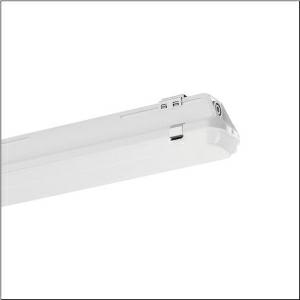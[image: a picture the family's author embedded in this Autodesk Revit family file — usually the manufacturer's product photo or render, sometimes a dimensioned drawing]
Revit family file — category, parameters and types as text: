
# Revit family: monsun_r__21_51fb107p480b_58b6
name_source: partatom
category: Lighting Fixtures
units: mm (PartAtom-declared; Revit-internal decimal feet)

## family parameters
Cut with Voids When Loaded = No
Host = Face
Light Source = No
Part Type = Normal
Room Calculation Point = No
Round Connector Dimension = Use Diameter
Shared = No

## types (1)
- Monsun® 21 (1 x LED, 8070 lm, 52.8 W, 4000K)
    Apparent Load = 53 VA
    CIE Flux Codes = 47 77 93 94 100
    Color Rendering = 80
    Color Temperature = 4000K
    Default Elevation = 1800 mm
    Description = Monsun® 21, damp-proof luminaire, chain hanger, primary optical cover: enclosure, of PMMA, light emission: direct distribution, primary light characteristic: symmetric, installation type: suspended mounting, surface-mounted, horizontal mounting, vertical mounting, LED, rated luminous flux: 8.070lm, luminous efficacy: 153lm/W, light colour: 840, colour temperature: 4000K, control gear: ECG, with terminal, 3-pole, max. 2.5mm², mains connection: 220..240V, AC, 50/60Hz, rated input power: 53W, housing, of glass-fibre reinforced polyester, uncoated, bright grey, length: 1.590mm, width: 90mm, height: 88mm, clip for enclosure, of stainless steel (V2A), ceiling mounting element, of stainless steel (V2A), chain hanger, of stainless steel (V2A), protection rating (complete): IP66, insulation class (complete): insulation class I (protective earthing), certification: CE, ENEC, VDE, UKCA, protection symbol: D, impact resistance: IK04, permissible operating ambient temperature: -25..+35°C, standard: EN 50419, EN 60598-2-1, corresponds to IFS (International Featured Standards) requirements for safety and quality in the food industry, for indoor or canopied outdoor use, no direct snow, no direct sun, no direct rain, packaging unit: 1 piece
    Height = 89 mm
    Lamp = 1 x LED
    Lamp Light Flux = 8070 lm
    Lamp Power = 52.8 W
    Lamp count = 1
    Length = 1590 mm
    Luminous efficacy = 153 lm/W
    Manufacturer = Siteco
    ModVariant = No
    Model = 51FB107P480B
    Mounting Place = Ceiling
    Mounting Type = Pendant
    Number of Poles = 1
    OnlyDefault = Yes
    Power Factor = 1
    Product Name = Monsun® 21
    Product group = damp-proof luminaire | ceiling pendant
    ProductGroupID = 908
    Protection Class = Protection class I
    Protection Degree = IP 66
    RLX_Detail_Level = 1
    RlxData = <blob elided: 88133 chars, md5=2f36a3cd>
    Socket = socket
    Standby Power = 0 W
    System Light Flux = 8070 lm
    System Power = 53 W
    Type Comments = Product without accessories
    Type Image = l_1006717.jpg
    URL = http://relux.com
    VarID = ---
    Voltage = 0 V
    Weight = 0.00 kg
    Width = 90 mm

## geometry (parser evidence)
native form markers: Blend x4, Sweep x13
no freeform markers — native parametric forms only
